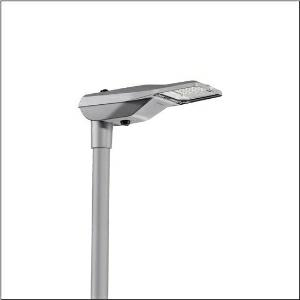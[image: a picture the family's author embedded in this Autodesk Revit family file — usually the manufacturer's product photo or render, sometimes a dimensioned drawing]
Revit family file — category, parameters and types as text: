
# Revit family: streetlight_sl_21_iq_micro___st1_5a_5xe1p31y08db_002f
name_source: partatom
category: Lighting Fixtures
units: mm (PartAtom-declared; Revit-internal decimal feet)

## family parameters
Cut with Voids When Loaded = No
Host = Face
Light Source = No
Part Type = Normal
Room Calculation Point = No
Round Connector Dimension = Use Diameter
Shared = No

## types (1)
- --- (1 x LED, 5030 lm, 39.1 W, 3000K)
    Apparent Load = 39 VA
    CIE Flux Codes = 22 53 95 100 100
    Color Rendering = 70
    Color Temperature = 3000K
    Default Elevation = 1800 mm
    Description = Streetlight SL 21 iQ micro, mast luminaire, primary light control with lens, of PMMA, primary optical cover: cover, of toughened safety glass, transparent, light distribution: ST1.5a, light emission: direct distribution, primary light characteristic: asymmetric, installation type: post-top, side-entry, LED, High Power LED, rated luminous flux: 5.030lm, luminous efficacy: 129lm/W, light colour: 730, colour temperature: 3000K, control gear: iQ-Street Remote, D4i with power reduction, control: pre-setting: logarithmic dimming characteristic, Street-Remote, Auto-Match, Temp-Guard, Lumen-Switch, Night-Set, Smart-Wire, Light-Fading, Desk-Remote (wireless, voltage-free reading and setting of iQ features in the workshop via application-optimized NFC function/RFID function), optimised constant luminous flux control (CLO 2.0), mains connection: 220..240V, AC, 50/60Hz, start of lifetime: 39W, end of service life: 41W, reduction: 17W, luminaire housing, of diecast aluminium, powder-coated, Siteco® metallic grey (DB 702S), corrosivity category C5 mid according to DIN EN ISO 12944, please order mast flange separately, inclination adjustable: 0°, 5°, 10°, 15°, sealing non-destructively replaceable, multi-level sealing system, length: 528mm, width: 235mm, height: 110mm, mast flange for spigot size: 42mm (side-entry): 5XC10008XM4, 60/48mm (side-entry/post-top): 5XC10108XM2, 76/60mm (side-entry/post-top): 5XC10108XM1, mounting height: 4..8m, Smart Interface below and above, protection rating (complete): IP66, insulation class (complete): insulation class II (safety insulation), certification: CE, ENEC, ENEC+, VDE, impact resistance: IK10, permissible operating ambient temperature for outdoor applications: -40..+50°C, standard-compliant lighting for roads and squares, packaging unit: 1 piece

Light Distribution: ST1.5a
    Height = 110 mm
    Lamp = 1 x LED
    Lamp Light Flux = 5030 lm
    Lamp Power = 39.1 W
    Lamp count = 1
    Length = 528 mm
    Luminous efficacy = 129 lm/W
    Manufacturer = Siteco
    ModVariant = No
    Model = 5XE1P31Y08DB
    Number of Poles = 1
    OnlyDefault = Yes
    Power Factor = 1
    Product Name = Streetlight SL 21 iQ micro | ST1.5a
    Product group = mast luminaire | pylon top
    ProductGroupID = 6100
    Protection Class = Protection class II
    Protection Degree = IP 66
    RLX_Detail_Level = 1
    RLX_Emergency_Light_Flux = 0 lm
    RLX_Emergency_Type = 0
    RLX_Emergency_Type_DB = No
    RlxData = <blob elided: 102853 chars, md5=a532bc9f>
    Socket = socket
    Standby Power = 0 W
    System Light Flux = 5030 lm
    System Power = 39 W
    Type Comments = factory setting: luminous flux: 100 % | dim-lin: 254 | 765 mA
    Type Image = l_1007239.jpg
    URL = http://relux.com
    VarID = @adj_133459
    Voltage = 0 V
    Weight = 0.00 kg
    Width = 235 mm

## geometry (parser evidence)
native form markers: Blend x4, Sweep x12
no freeform markers — native parametric forms only
